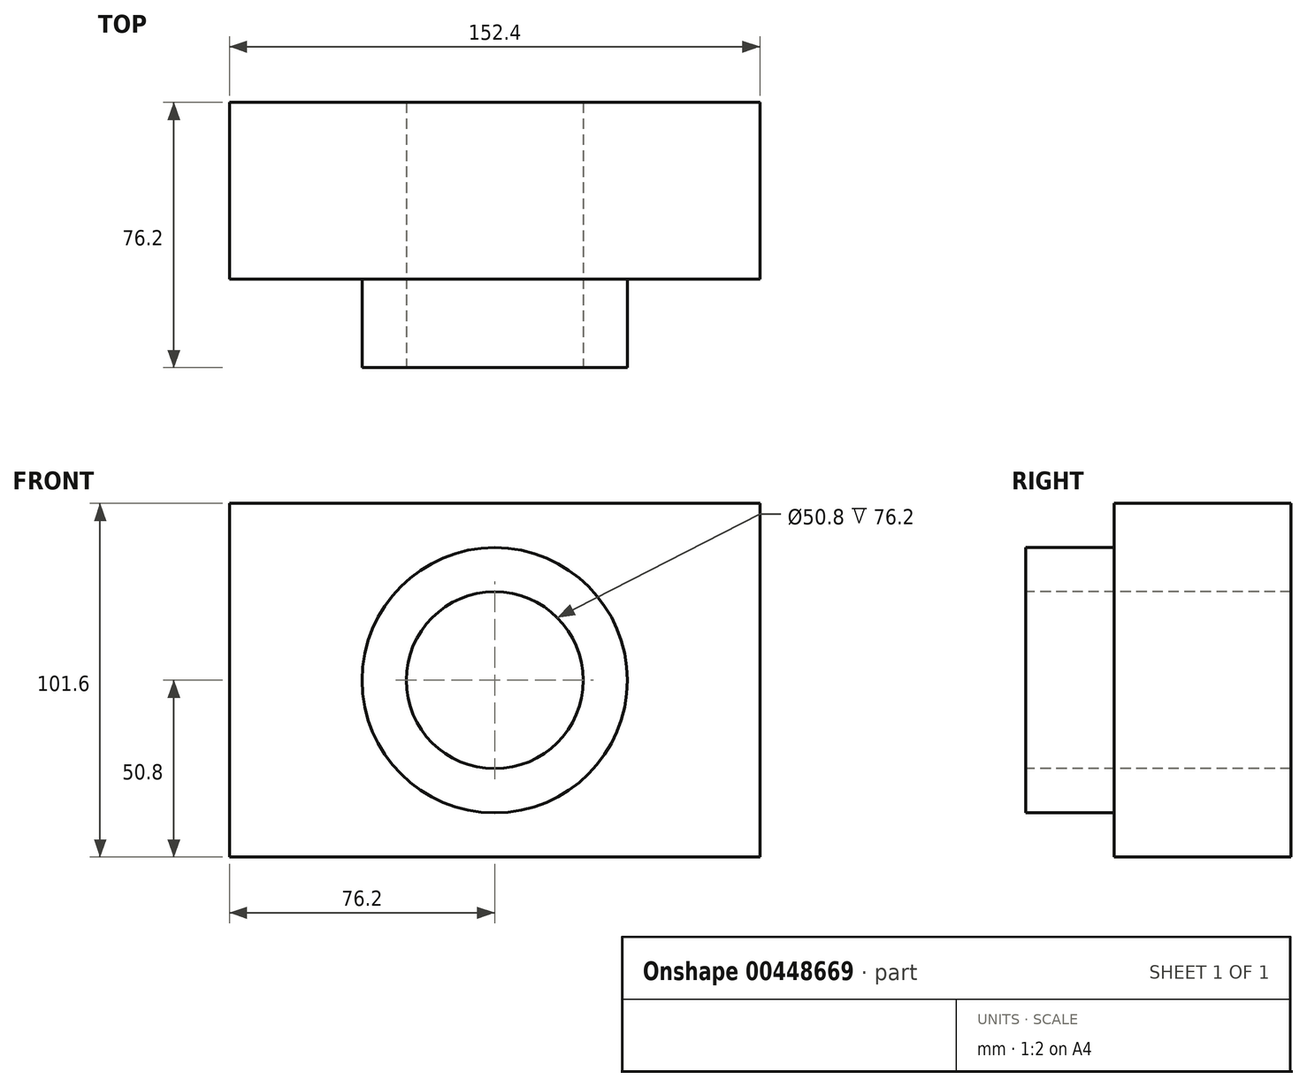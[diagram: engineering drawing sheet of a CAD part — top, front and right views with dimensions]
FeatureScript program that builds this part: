
annotation { "Feature Type Name" : "Feature", "Feature Type Description" : "" }
export const myFeature = defineFeature(function(context is Context, id is Id, definition is map)
    precondition{}
    {
        {
            var Q0;
            Q0=qCreatedBy(makeId("Front.planeOp"),FACE);
            var sketch = newSketch(context, id + "F0", { "sketchPlane" : qUnion([Q0])});
            skLineSegment(sketch, "E0.bottom", {"start": v(76.2, 50.8) * mm, "end": v(-76.2, 50.8) * mm});
            skLineSegment(sketch, "E0.top", {"start": v(76.2, -50.8) * mm, "end": v(-76.2, -50.8) * mm});
            skLineSegment(sketch, "E0.left", {"start": v(76.2, 50.8) * mm, "end": v(76.2, -50.8) * mm});
            skLineSegment(sketch, "E0.right", {"start": v(-76.2, 50.8) * mm, "end": v(-76.2, -50.8) * mm});
            skPoint(sketch, "E0.middle", {"position": v(0, 0) * mm});
            skSolve(sketch);
        }
        {
            var Q0;
            Q0=makeQuery(id+"F0.imprint","IMPRINT",FACE,{"disambiguationData":[TD([[makeQuery(id+"F0.imprint","IMPRINT",EDGE,{"derivedFrom":sQuery(id+"F0.wireOp",EDGE,"E0.bottom")}),1.0]])]});
            extrude(context, id + "F1", {"entities" : qUnion([Q0]), "endBound" : BoundingType.SYMMETRIC, "depth" : 50.8 * mm});
        }
        {
            var Q0;
            Q0=makeQuery(id+"F1.opExtrude","CAP_FACE",FACE,{"disambiguationData":[OSD([sQuery(id+"F0.wireOp",EDGE,"E0.bottom"),sQuery(id+"F0.wireOp",EDGE,"E0.top"),sQuery(id+"F0.wireOp",EDGE,"E0.left"),sQuery(id+"F0.wireOp",EDGE,"E0.right")])],"isStart":false});
            var sketch = newSketch(context, id + "F2", { "sketchPlane" : qUnion([Q0])});
            skCircle(sketch, "E1", {"center": v(0, 0) * mm, "radius": 38.1 * mm});
            skSolve(sketch);
        }
        {
            var Q0;
            Q0=makeQuery(id+"F2.imprint","IMPRINT",FACE,{"disambiguationData":[TD([[makeQuery(id+"F2.imprint","IMPRINT",EDGE,{"derivedFrom":sQuery(id+"F2.wireOp",EDGE,"E1")}),1.0]])]});
            extrude(context, id + "F3", {"entities" : qUnion([Q0]), "operationType" : NewBodyOperationType.ADD, "depth" : 25.4 * mm});
        }
        {
            var Q0;
            Q0=makeQuery(id+"F3.opExtrude","CAP_FACE",FACE,{"disambiguationData":[OSD([sQuery(id+"F2.wireOp",EDGE,"E1")])],"isStart":false});
            var sketch = newSketch(context, id + "F4", { "sketchPlane" : qUnion([Q0])});
            skCircle(sketch, "E2", {"center": v(0, 0) * mm, "radius": 25.4 * mm});
            skSolve(sketch);
        }
        {
            var Q0;
            Q0=makeQuery(id+"F4.imprint","IMPRINT",FACE,{"disambiguationData":[TD([[makeQuery(id+"F4.imprint","IMPRINT",EDGE,{"derivedFrom":sQuery(id+"F4.wireOp",EDGE,"E2")}),1.0]])]});
            extrude(context, id + "F5", {"entities" : qUnion([Q0]), "operationType" : NewBodyOperationType.REMOVE, "endBound" : BoundingType.THROUGH_ALL, "oppositeDirection" : true, "depth" : 25.4 * mm});
        }
    });
